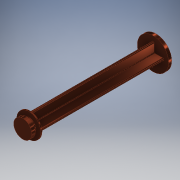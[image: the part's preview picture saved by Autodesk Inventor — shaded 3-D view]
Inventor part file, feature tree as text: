
AUTODESK INVENTOR PART (.ipt)
format: ipt  version: 2018 (Build 220112000, 112)  size: 222,208 bytes
history: native  units: mm
features: sketch x4, extrude x3, revolve x1, fillet x1
ambient origin geometry x8: Origin, YZ Plane, XZ Plane, XY Plane, X Axis, Y Axis, Z Axis, Center Point
bodies: Solid1 (feature_tree)
feature tree (9):
  revolve  "Revolution1"  [1 undecoded]
  extrude  "Extrusion1"  Depth=2.0mm
  extrude  "Extrusion2"  Depth=7.5mm
  extrude  "Extrusion3"  Depth=1.0mm
  fillet  "Fillet1"  Radius=1.0mm
  sketch  "Sketch1"  dims[d0=10.0mm d1=6.0mm]
  sketch  "Sketch2"  dims[d2=1.0mm d3=2.0mm]
  sketch  "Sketch3"  dims[d4=3.0mm d5=7.5mm]
  sketch  "Sketch4"  dims[d6=90.0deg d7=1.0mm d8=1.0mm d9=1.0mm d10=1.0mm d11=8.0mm d16=8.0mm d17=8.0mm d18=8.0mm d19=0.5mm d20=102.0mm d21=0.0mm d22=26.0mm d23=2.5mm d24=0.0mm d25=1.5mm d26=1.5mm d27=10.0mm d28=10.0mm d29=1.2mm d30=3.0mm d31=8.0mm d32=8.0mm d33=1.2mm d34=6.0mm d35=6.0mm d36=3.0mm d37=1.2mm d38=8.0mm d39=8.0mm d40=3.0mm d41=1.2mm d42=3.0mm d43=6.0mm d44=6.0mm d45=1.0mm d46=0.0mm d47=1.0mm]
note: 1 required parameter value undecoded (feature->parameter linkage not recoverable at this tier; creation-order binding heuristic only, values carry confidence <= 0.55)
